# Revit family: BDG_BossDeisgn_Stng_ATOM_Booths_ModelCodeUpdated_29.01
name_source: partatom
category: Furniture
revit_build: Autodesk Revit 2016 (Build: 20150220_1215(x64)
units: mm (PartAtom-declared; Revit-internal decimal feet)

## family parameters
Always vertical = Yes
Cut with Voids When Loaded = No
Room Calculation Point = No
Shared = Yes
Work Plane-Based = No

## types (2) — shared parameters
Assembly Code = E2020200
AssetType = Movable
BIMObjectName = BDG_BossDesign_Seating_ATOM_Booths
Category = Pr_40_50_12 : Chairs, seats and benches
Color = Various
Description = ATOM Booth
DurationUnit = year
ExpectedLife = 5
Finish = Fabric
IfcExportAs = IfcFurnishingElementType
IfcExportType = SOFA
IsB001 = No
Keynote = Pr_40_50_12
MainColor = Various
ManufacturerName = Boss Design
ManufacturerURL = www.bossdesign.com
Material = Upholstered
ModelReference = ATOM Booth
NBSDescription = Seating
NBSReference = 45-35-72/352
Name = Seating_ATOM_Booths_BossDesign
NominalHeight = 1390 mm  [stored 4.56037 ft]
NominalLength = 2795 mm  [stored 9.16995 ft]
NominalWidth = 2200 mm
Shape = Rectangular
Size = 2795 x 2200 x 1390mm
URL = www.bossdesign.com
Uniclass2015Code = Pr_40_50_12
Uniclass2015Title = Chairs, seats and benches
Uniclass2015Version = Products v1.8
Version = 1
WarrantyDescription = Structural Warranty Excludes Foams and Fabrics
WarrantyDurationLabor = 5
WarrantyDurationParts = 5
WarrantyDurationUnit = year

## per-type parameters (varying)
| type | IsATO00H | IsATOHB |
| ATO/B001/H | Yes | No |
| ATO/B001/H/B | No | Yes |

note: column(s) folded — value = type name in every type: Model, ModelNumber

note: [stored X ft] marks values corroborated as IEEE doubles in the binary element streams (Revit-internal decimal feet)

## geometry (parser evidence)
native form markers: Sweep x6
no freeform markers — native parametric forms only
